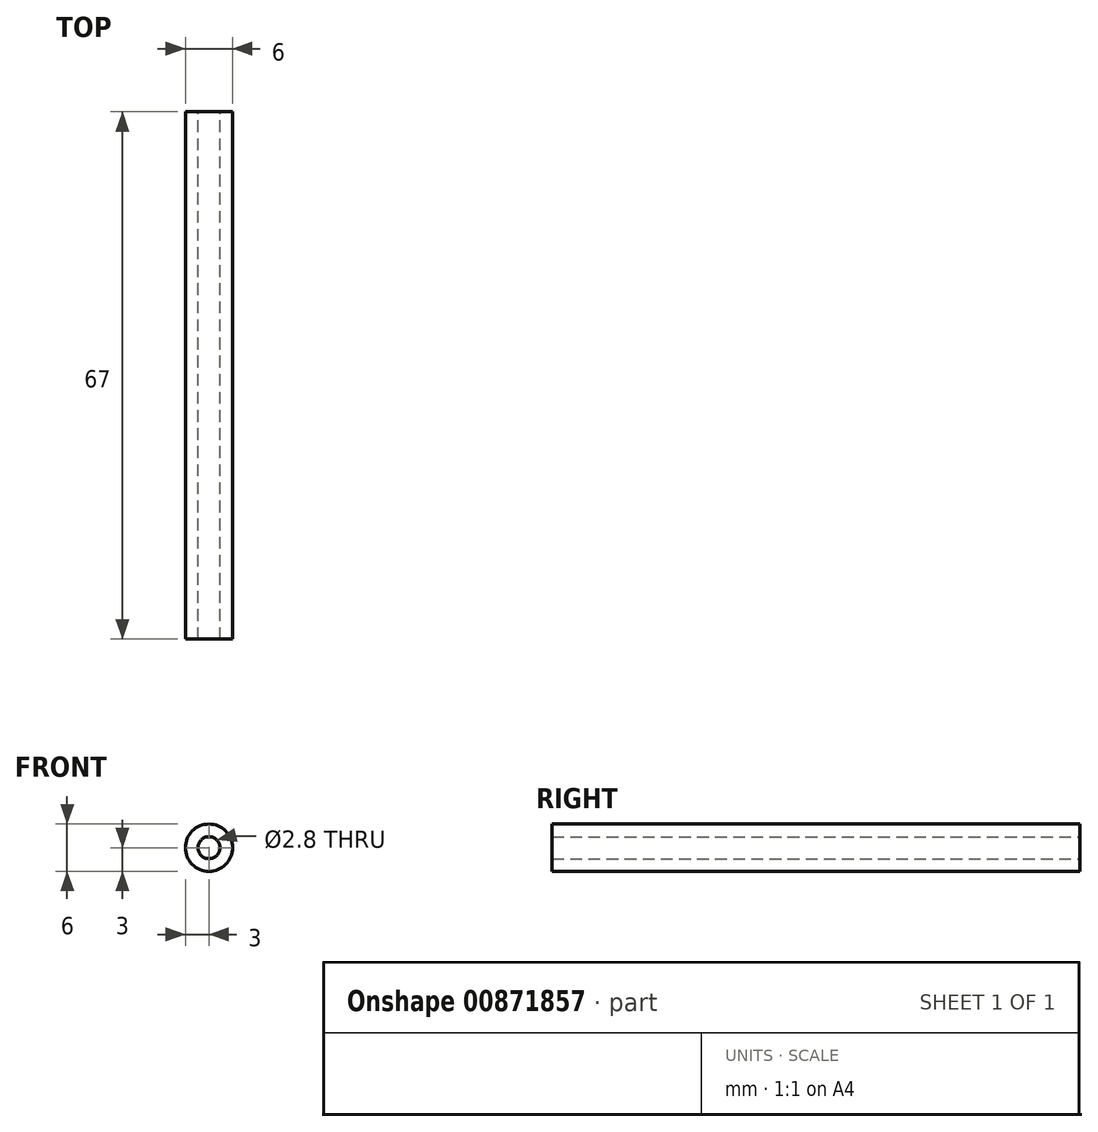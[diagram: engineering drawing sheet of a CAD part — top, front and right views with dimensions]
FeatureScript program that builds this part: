
annotation { "Feature Type Name" : "Feature", "Feature Type Description" : "" }
export const myFeature = defineFeature(function(context is Context, id is Id, definition is map)
    precondition{}
    {
        {
            var Q0;
            Q0=qCreatedBy(makeId("Front.planeOp"),FACE);
            var sketch = newSketch(context, id + "F0", { "sketchPlane" : qUnion([Q0])});
            skCircle(sketch, "E0", {"center": v(0, 0) * mm, "radius": 3 * mm});
            skCircle(sketch, "E1", {"center": v(0, 0) * mm, "radius": 1.4 * mm});
            skSolve(sketch);
        }
        {
            var Q0;
            Q0=makeQuery(id+"F0.imprint","IMPRINT",FACE,{"disambiguationData":[TD([[makeQuery(id+"F0.imprint","IMPRINT",EDGE,{"derivedFrom":sQuery(id+"F0.wireOp",EDGE,"E0")}),1.0]])]});
            extrude(context, id + "F1", {"entities" : qUnion([Q0]), "depth" : 67 * mm, "offsetDistance" : 25 * mm});
        }
    });
